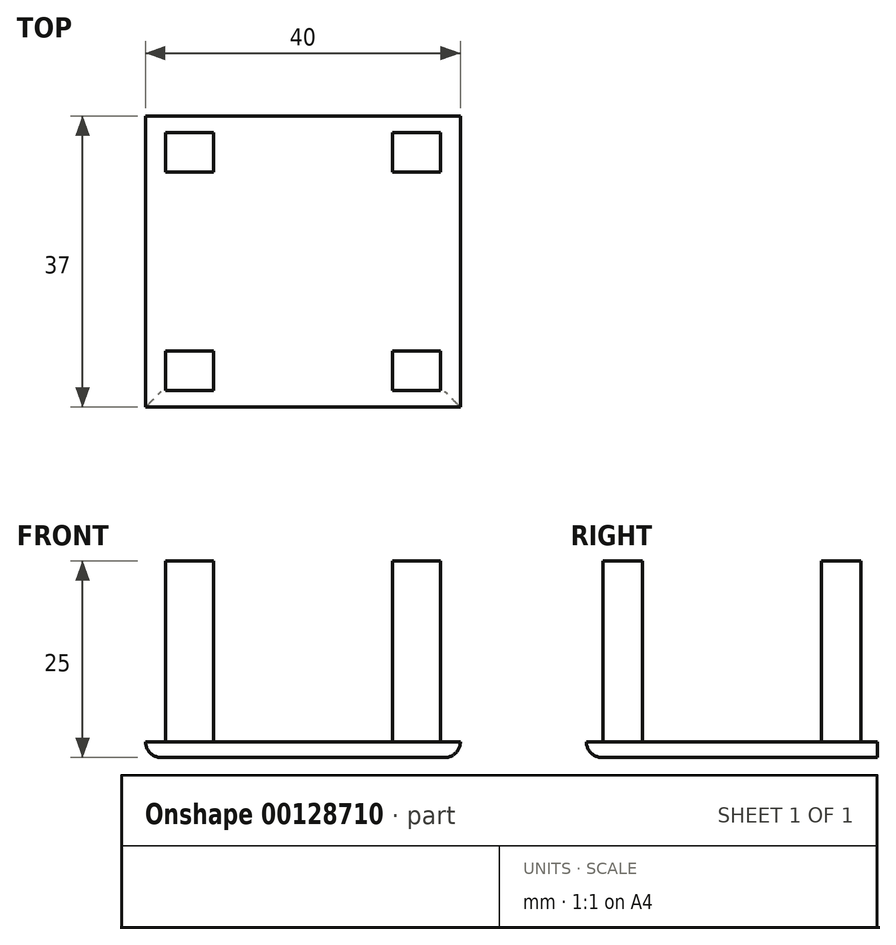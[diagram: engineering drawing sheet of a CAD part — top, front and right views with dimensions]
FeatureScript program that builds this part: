
annotation { "Feature Type Name" : "Feature", "Feature Type Description" : "" }
export const myFeature = defineFeature(function(context is Context, id is Id, definition is map)
    precondition{}
    {
        {
            var Q0;
            Q0=qCreatedBy(makeId("Top.planeOp"),FACE);
            var sketch = newSketch(context, id + "F0", { "sketchPlane" : qUnion([Q0])});
            skLineSegment(sketch, "E0.bottom", {"start": v(-20, 18.5) * mm, "end": v(20, 18.5) * mm});
            skLineSegment(sketch, "E0.top", {"start": v(-20, -18.5) * mm, "end": v(20, -18.5) * mm});
            skLineSegment(sketch, "E0.left", {"start": v(-20, 18.5) * mm, "end": v(-20, -18.5) * mm});
            skLineSegment(sketch, "E0.right", {"start": v(20, 18.5) * mm, "end": v(20, -18.5) * mm});
            skPoint(sketch, "E0.middle", {"position": v(0, 0) * mm});
            skLineSegment(sketch, "E1.top", {"start": v(-20, 13.7) * mm, "end": v(20, 13.7) * mm});
            skLineSegment(sketch, "E1.left", {"start": v(-20, 18.5) * mm, "end": v(-20, 13.7) * mm});
            skLineSegment(sketch, "E1.right", {"start": v(20, 18.5) * mm, "end": v(20, 13.7) * mm});
            skLineSegment(sketch, "E2.bottom", {"start": v(17.45, 11.38) * mm, "end": v(11.36, 11.38) * mm});
            skLineSegment(sketch, "E2.top", {"start": v(17.45, 16.38) * mm, "end": v(11.36, 16.38) * mm});
            skLineSegment(sketch, "E2.left", {"start": v(17.45, 11.38) * mm, "end": v(17.45, 16.38) * mm});
            skLineSegment(sketch, "E2.right", {"start": v(11.36, 11.38) * mm, "end": v(11.36, 16.38) * mm});
            skLineSegment(sketch, "E3.MirrorCS", {"start": v(-17.45, 11.38) * mm, "end": v(-11.36, 11.38) * mm});
            skLineSegment(sketch, "E4.MirrorCS", {"start": v(-11.36, 11.38) * mm, "end": v(-11.36, 16.38) * mm});
            skLineSegment(sketch, "E5.MirrorCS", {"start": v(-17.45, 11.38) * mm, "end": v(-17.45, 16.38) * mm});
            skLineSegment(sketch, "E6.MirrorCS", {"start": v(-17.45, 16.38) * mm, "end": v(-11.36, 16.38) * mm});
            skLineSegment(sketch, "E7.MirrorCS", {"start": v(17.45, -11.38) * mm, "end": v(11.36, -11.38) * mm});
            skLineSegment(sketch, "E8.MirrorCS", {"start": v(11.36, -11.38) * mm, "end": v(11.36, -16.38) * mm});
            skLineSegment(sketch, "E9.MirrorCS", {"start": v(17.45, -16.38) * mm, "end": v(11.36, -16.38) * mm});
            skLineSegment(sketch, "E10.MirrorCS", {"start": v(17.45, -11.38) * mm, "end": v(17.45, -16.38) * mm});
            skLineSegment(sketch, "E11.MirrorCS", {"start": v(-17.45, -11.38) * mm, "end": v(-11.36, -11.38) * mm});
            skLineSegment(sketch, "E12.MirrorCS", {"start": v(-17.45, -16.38) * mm, "end": v(-11.36, -16.38) * mm});
            skLineSegment(sketch, "E13.MirrorCS", {"start": v(-11.36, -11.38) * mm, "end": v(-11.36, -16.38) * mm});
            skLineSegment(sketch, "E14.MirrorCS", {"start": v(-17.45, -11.38) * mm, "end": v(-17.45, -16.38) * mm});
            skSolve(sketch);
        }
        {
            var Q0;
            {var subQ5=sQuery(id+"F0.wireOp",EDGE,"E6.MirrorCS");Q0=makeQuery(id+"F0.imprint","IMPRINT",FACE,{"disambiguationData":[TD([[makeQuery(id+"F0.imprint","IMPRINT",EDGE,{"derivedFrom":subQ5}),-1.0]])]});}
            var Q1;
            {var subQ5=sQuery(id+"F0.wireOp",EDGE,"E2.bottom");Q1=makeQuery(id+"F0.imprint","IMPRINT",FACE,{"disambiguationData":[TD([[makeQuery(id+"F0.imprint","IMPRINT",EDGE,{"derivedFrom":subQ5}),-1.0]])]});}
            var Q2;
            Q2=makeQuery(id+"F0.imprint","IMPRINT",FACE,{"disambiguationData":[TD([[makeQuery(id+"F0.imprint","IMPRINT",EDGE,{"derivedFrom":sQuery(id+"F0.wireOp",EDGE,"E7.MirrorCS")}),1.0]])]});
            var Q3;
            Q3=makeQuery(id+"F0.imprint","IMPRINT",FACE,{"disambiguationData":[TD([[makeQuery(id+"F0.imprint","IMPRINT",EDGE,{"derivedFrom":sQuery(id+"F0.wireOp",EDGE,"E11.MirrorCS")}),-1.0]])]});
            var Q4;
            {var subQ5=sQuery(id+"F0.wireOp",EDGE,"E2.top");Q4=makeQuery(id+"F0.imprint","IMPRINT",FACE,{"disambiguationData":[TD([[makeQuery(id+"F0.imprint","IMPRINT",EDGE,{"derivedFrom":subQ5}),1.0]])]});}
            var Q5;
            Q5=makeQuery(id+"F0.imprint","IMPRINT",FACE,{"disambiguationData":[TD([[makeQuery(id+"F0.imprint","IMPRINT",EDGE,{"derivedFrom":sQuery(id+"F0.wireOp",EDGE,"E0.bottom")}),-1.0]])]});
            var Q6;
            {var subQ5=sQuery(id+"F0.wireOp",EDGE,"E3.MirrorCS");Q6=makeQuery(id+"F0.imprint","IMPRINT",FACE,{"disambiguationData":[TD([[makeQuery(id+"F0.imprint","IMPRINT",EDGE,{"derivedFrom":subQ5}),1.0]])]});}
            var Q7;
            Q7=makeQuery(id+"F0.imprint","IMPRINT",FACE,{"disambiguationData":[TD([[makeQuery(id+"F0.imprint","IMPRINT",EDGE,{"derivedFrom":sQuery(id+"F0.wireOp",EDGE,"E0.top")}),1.0]])]});
            extrude(context, id + "F1", {"entities" : qUnion([Q0, Q1, Q2, Q3, Q4, Q5, Q6, Q7]), "depth" : 2 * mm});
        }
        {
            var Q0;
            Q0=makeQuery(id+"F0.imprint","IMPRINT",FACE,{"disambiguationData":[TD([[makeQuery(id+"F0.imprint","IMPRINT",EDGE,{"derivedFrom":sQuery(id+"F0.wireOp",EDGE,"E7.MirrorCS")}),1.0]])]});
            var Q1;
            {var subQ5=sQuery(id+"F0.wireOp",EDGE,"E2.bottom");Q1=makeQuery(id+"F0.imprint","IMPRINT",FACE,{"disambiguationData":[TD([[makeQuery(id+"F0.imprint","IMPRINT",EDGE,{"derivedFrom":subQ5}),-1.0]])]});}
            var Q2;
            {var subQ5=sQuery(id+"F0.wireOp",EDGE,"E2.top");Q2=makeQuery(id+"F0.imprint","IMPRINT",FACE,{"disambiguationData":[TD([[makeQuery(id+"F0.imprint","IMPRINT",EDGE,{"derivedFrom":subQ5}),1.0]])]});}
            var Q3;
            {var subQ5=sQuery(id+"F0.wireOp",EDGE,"E3.MirrorCS");Q3=makeQuery(id+"F0.imprint","IMPRINT",FACE,{"disambiguationData":[TD([[makeQuery(id+"F0.imprint","IMPRINT",EDGE,{"derivedFrom":subQ5}),1.0]])]});}
            var Q4;
            {var subQ5=sQuery(id+"F0.wireOp",EDGE,"E6.MirrorCS");Q4=makeQuery(id+"F0.imprint","IMPRINT",FACE,{"disambiguationData":[TD([[makeQuery(id+"F0.imprint","IMPRINT",EDGE,{"derivedFrom":subQ5}),-1.0]])]});}
            var Q5;
            Q5=makeQuery(id+"F0.imprint","IMPRINT",FACE,{"disambiguationData":[TD([[makeQuery(id+"F0.imprint","IMPRINT",EDGE,{"derivedFrom":sQuery(id+"F0.wireOp",EDGE,"E11.MirrorCS")}),-1.0]])]});
            extrude(context, id + "F2", {"entities" : qUnion([Q0, Q1, Q2, Q3, Q4, Q5]), "operationType" : NewBodyOperationType.ADD, "depth" : 25 * mm});
        }
        {
            var Q0;
            Q0=sQuery(id+"F0.wireOp",EDGE,"E1.top");
            var Q1;
            Q1=sQuery(id+"F0.wireOp",EDGE,"E1.left");
            var Q2;
            Q2=sQuery(id+"F0.wireOp",EDGE,"E0.bottom");
            var Q3;
            Q3=sQuery(id+"F0.wireOp",EDGE,"E1.right");
            extrude(context, id + "F3", {"bodyType" : ToolBodyType.SURFACE, "operationType" : NewBodyOperationType.ADD, "surfaceEntities" : qUnion([Q0, Q1, Q2, Q3]), "oppositeDirection" : true, "depth" : 25 * mm});
        }
        {
            var Q0;
            Q0=makeQuery(id+"F1.opExtrude","CAP_EDGE",EDGE,{"disambiguationData":[OSD([sQuery(id+"F0.wireOp",EDGE,"E0.right"),sQuery(id+"F0.wireOp",EDGE,"E1.right")])],"isStart":true});
            var Q1;
            Q1=makeQuery(id+"F1.opExtrude","CAP_EDGE",EDGE,{"disambiguationData":[OSD([sQuery(id+"F0.wireOp",EDGE,"E0.left"),sQuery(id+"F0.wireOp",EDGE,"E1.left")])],"isStart":true});
            var Q2;
            Q2=makeQuery(id+"F3.opExtrude","SWEPT_EDGE",EDGE,{"disambiguationData":[OSD([sQuery(id+"F0.wireOp",VERTEX,"E1.left.end")])]});
            var Q3;
            Q3=makeQuery(id+"F3.opExtrude","SWEPT_EDGE",EDGE,{"disambiguationData":[OSD([sQuery(id+"F0.wireOp",VERTEX,"E1.right.end")])]});
            var Q4;
            Q4=makeQuery(id+"F1.opExtrude","CAP_EDGE",EDGE,{"disambiguationData":[OSD([sQuery(id+"F0.wireOp",EDGE,"E0.top")])],"isStart":true});
            var Q5;
            Q5=makeQuery(id+"F3.opExtrude","SWEPT_EDGE",EDGE,{"disambiguationData":[OSD([sQuery(id+"F0.wireOp",VERTEX,"E0.bottom.start")])]});
            var Q6;
            Q6=makeQuery(id+"F3.opExtrude","SWEPT_EDGE",EDGE,{"disambiguationData":[OSD([sQuery(id+"F0.wireOp",VERTEX,"E1.right.start")])]});
            fillet(context, id + "F4", {"entities" : qUnion([Q0, Q1, Q2, Q3, Q4, Q5, Q6]), "radius" : 2 * mm, "tangentPropagation" : true, "allowEdgeOverflow" : false});
        }
        {
            var Q0;
            Q0=makeQuery(id+"F3.opExtrude","SWEPT_FACE",FACE,{"disambiguationData":[OSD([sQuery(id+"F0.wireOp",EDGE,"E1.top")])]});
            var sketch = newSketch(context, id + "F5", { "sketchPlane" : qUnion([Q0])});
            skCircle(sketch, "E15", {"center": v(0, -14.48) * mm, "radius": 6.3 * mm});
            skSolve(sketch);
        }
        {
            var Q0;
            Q0=makeQuery(id+"F5.imprint","IMPRINT",FACE,{"disambiguationData":[TD([[makeQuery(id+"F5.imprint","IMPRINT",EDGE,{"derivedFrom":sQuery(id+"F5.wireOp",EDGE,"E15")}),1.0]])]});
            extrude(context, id + "F6", {"entities" : qUnion([Q0]), "operationType" : NewBodyOperationType.REMOVE, "endBound" : BoundingType.UP_TO_NEXT, "depth" : 25 * mm});
        }
    });
